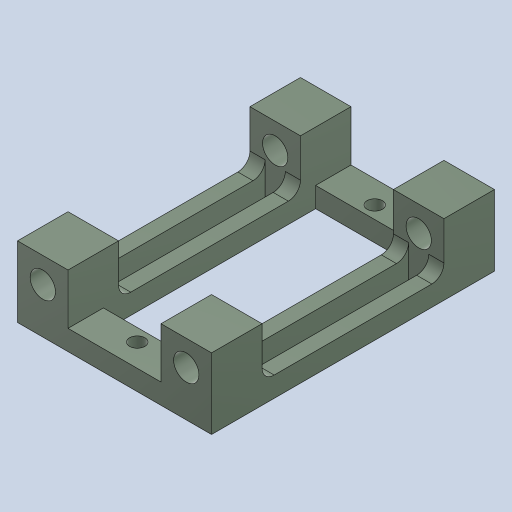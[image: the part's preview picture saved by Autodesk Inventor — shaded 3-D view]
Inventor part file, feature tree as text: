
AUTODESK INVENTOR PART (.ipt)
format: ipt  version: 2023 (Build 270158000, 158)  size: 231,936 bytes
history: native  units: in
note: dims shown in document units (in); Inventor stores cm internally (conversion verified against a paired STEP export)
features: sketch x4, extrude x4, other x3, mirror x2, hole x1, fillet x1, projected_geometry x1
ambient origin geometry x8: Origin, YZ Plane, XZ Plane, XY Plane, X Axis, Y Axis, Z Axis, Center Point
bodies: Body1 (feature_tree)
feature tree (16):
  other  "ソリッド1"
  sketch  "スケッチ1"
  extrude  "押し出し1"  Depth=0.8268in
  hole  "穴1"  [1 undecoded]
  extrude  "押し出し2"  Depth=0.1969in
  extrude  "押し出し5"  Depth=0.9252in
  mirror  "ミラー4"
  extrude  "押し出し6"  Depth=0.315in
  mirror  "ミラー5"
  fillet  "フィレット1"  Radius=0.0787in
  other  "作業平面1"
  other  "作業平面2"
  sketch  "スケッチ2"
  projected_geometry  "投影ループ1"
  sketch  "スケッチ6"
  sketch  "スケッチ7"
note: 1 required parameter value undecoded (feature->parameter linkage not recoverable at this tier; creation-order binding heuristic only, values carry confidence <= 0.55)
